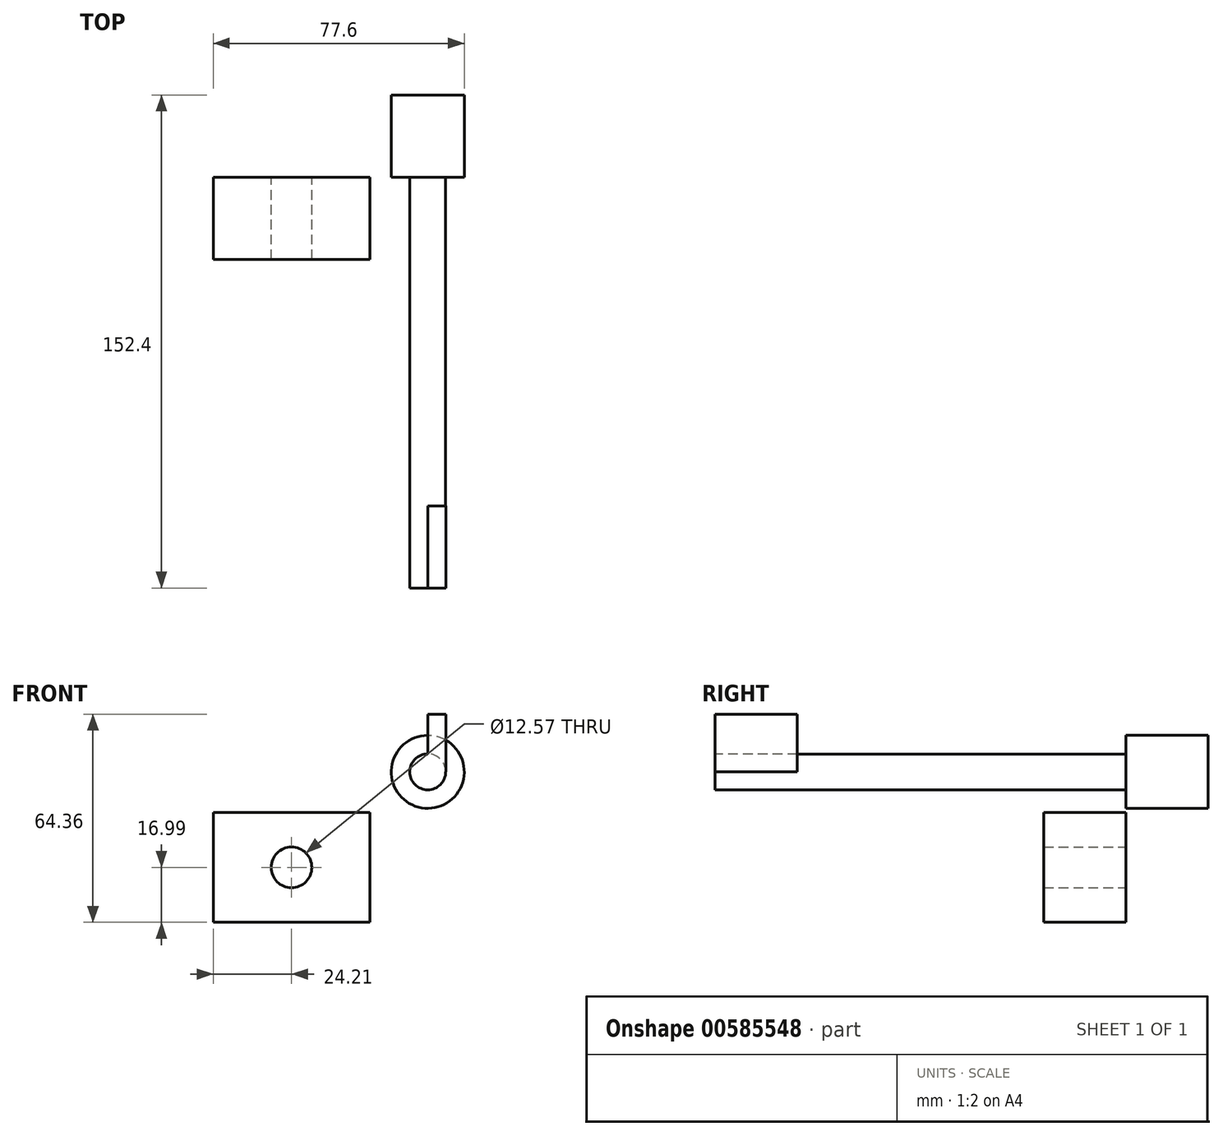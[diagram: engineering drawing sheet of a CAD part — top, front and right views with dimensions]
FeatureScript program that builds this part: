
annotation { "Feature Type Name" : "Feature", "Feature Type Description" : "" }
export const myFeature = defineFeature(function(context is Context, id is Id, definition is map)
    precondition{}
    {
        {
            var Q0;
            Q0=qCreatedBy(makeId("Front.planeOp"),FACE);
            var sketch = newSketch(context, id + "F0", { "sketchPlane" : qUnion([Q0])});
            skLineSegment(sketch, "E0.bottom", {"start": v(-24.21, 17) * mm, "end": v(24.21, 17) * mm});
            skLineSegment(sketch, "E0.top", {"start": v(-24.21, -17) * mm, "end": v(24.21, -17) * mm});
            skLineSegment(sketch, "E0.left", {"start": v(-24.21, 17) * mm, "end": v(-24.21, -17) * mm});
            skLineSegment(sketch, "E0.right", {"start": v(24.21, 17) * mm, "end": v(24.21, -17) * mm});
            skPoint(sketch, "E0.middle", {"position": v(0, 0) * mm});
            skCircle(sketch, "E1", {"center": v(0, 0) * mm, "radius": 6.28 * mm});
            skSolve(sketch);
        }
        {
            var Q0;
            Q0 = qSketchRegion(id + "F0", true);
            extrude(context, id + "F1", {"entities" : qUnion([Q0]), "depth" : 25.4 * mm, "offsetDistance" : 25.4 * mm});
        }
        {
            var Q0;
            Q0=qCreatedBy(makeId("Front.planeOp"),FACE);
            var sketch = newSketch(context, id + "F2", { "sketchPlane" : qUnion([Q0])});
            skCircle(sketch, "E2", {"center": v(42.11, 29.52) * mm, "radius": 5.55 * mm});
            skLineSegment(sketch, "E3.bottom", {"start": v(42.11, 29.52) * mm, "end": v(47.68, 29.52) * mm});
            skLineSegment(sketch, "E3.top", {"start": v(42.11, 46.17) * mm, "end": v(47.68, 46.17) * mm});
            skLineSegment(sketch, "E3.left", {"start": v(42.11, 29.52) * mm, "end": v(42.11, 46.17) * mm});
            skLineSegment(sketch, "E3.right", {"start": v(47.68, 29.52) * mm, "end": v(47.68, 46.17) * mm});
            skSolve(sketch);
        }
        {
            var Q0;
            Q0=makeQuery(id+"F2.imprint","IMPRINT",FACE,{"disambiguationData":[TD([[makeQuery(id+"F2.imprint","IMPRINT",EDGE,{"derivedFrom":sQuery(id+"F2.wireOp",EDGE,"E2")}),1.0]])]});
            extrude(context, id + "F3", {"entities" : qUnion([Q0]), "depth" : 127 * mm, "offsetDistance" : 25.4 * mm});
        }
        {
            var Q0;
            Q0=makeQuery(id+"F3.opExtrude","CAP_FACE",FACE,{"disambiguationData":[OSD([sQuery(id+"F2.wireOp",EDGE,"E2")])],"isStart":false});
            var sketch = newSketch(context, id + "F4", { "sketchPlane" : qUnion([Q0])});
            skLineSegment(sketch, "E4.bottom", {"start": v(42.11, 29.52) * mm, "end": v(47.68, 29.52) * mm});
            skLineSegment(sketch, "E4.top", {"start": v(42.11, 47.37) * mm, "end": v(47.68, 47.37) * mm});
            skLineSegment(sketch, "E4.left", {"start": v(42.11, 29.52) * mm, "end": v(42.11, 47.37) * mm});
            skLineSegment(sketch, "E4.right", {"start": v(47.68, 29.52) * mm, "end": v(47.68, 47.37) * mm});
            skSolve(sketch);
        }
        {
            var Q0;
            {var subQ2=sQuery(id+"F4.wireOp",EDGE,"E4.top");Q0=makeQuery(id+"F4.imprint","IMPRINT",FACE,{"disambiguationData":[TD([[makeQuery(id+"F4.imprint","IMPRINT",EDGE,{"derivedFrom":subQ2}),-1.0]])]});}
            extrude(context, id + "F5", {"entities" : qUnion([Q0]), "operationType" : NewBodyOperationType.ADD, "depth" : 0 * mm, "offsetDistance" : 25.4 * mm, "hasSecondDirection" : true, "secondDirectionOppositeDirection" : true, "secondDirectionDepth" : 25.4 * mm});
        }
        {
            var Q0;
            Q0=makeQuery(id+"F3.opExtrude","CAP_FACE",FACE,{"disambiguationData":[OSD([sQuery(id+"F2.wireOp",EDGE,"E2")])],"isStart":true});
            var sketch = newSketch(context, id + "F6", { "sketchPlane" : qUnion([Q0])});
            skCircle(sketch, "E5", {"center": v(-42.11, 29.52) * mm, "radius": 11.28 * mm});
            skSolve(sketch);
        }
        {
            var Q0;
            Q0=makeQuery(id+"F6.imprint","IMPRINT",FACE,{"disambiguationData":[TD([[makeQuery(id+"F6.imprint","IMPRINT",EDGE,{"derivedFrom":makeQuery(id+"F3.opExtrude","CAP_EDGE",EDGE,{"disambiguationData":[OSD([sQuery(id+"F2.wireOp",EDGE,"E2")])],"isStart":true})}),-1.0]])]});
            var Q1;
            Q1=makeQuery(id+"F6.imprint","IMPRINT",FACE,{"disambiguationData":[TD([[makeQuery(id+"F6.imprint","IMPRINT",EDGE,{"derivedFrom":sQuery(id+"F6.wireOp",EDGE,"E5")}),1.0]])]});
            extrude(context, id + "F7", {"entities" : qUnion([Q0, Q1]), "operationType" : NewBodyOperationType.ADD, "depth" : 25.4 * mm, "offsetDistance" : 25.4 * mm});
        }
    });
